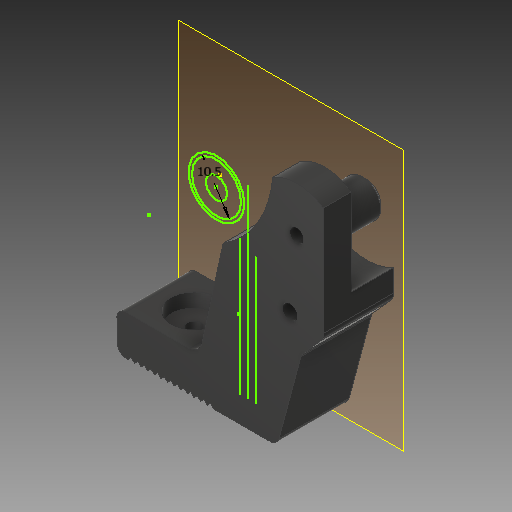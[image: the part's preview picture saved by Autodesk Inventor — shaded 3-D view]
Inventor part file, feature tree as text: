
AUTODESK INVENTOR PART (.ipt)
format: ipt  version: 2018 (Build 220112000, 112)  size: 333,824 bytes
history: native  units: in
note: dims shown in document units (in); Inventor stores cm internally (conversion verified against a paired STEP export)
features: extrude x10, sketch x10, fillet x2, reference x2, plane x1, chamfer x1, projected_geometry x1, other x1
ambient origin geometry x8: Origin, YZ Plane, XZ Plane, XY Plane, X Axis, Y Axis, Z Axis, Center Point
bodies: Solid1 (feature_tree)
feature tree (28):
  plane  "Work Plane1"
  extrude  "Extrusion1"  Depth=0.0787in
  sketch  "Sketch2"  dims[d2=0.0787in d4=0.126in]
  extrude  "Extrusion2"  Depth=0.126in
  chamfer  "Chamfer1"  Distance=0.0394in
  extrude  "Extrusion3"  Depth=0.0394in
  fillet  "Fillet1"  Radius=0.0394in
  extrude  "Extrusion4"  Depth=0.0394in
  extrude  "Extrusion5"  Depth=0.0394in
  extrude  "Extrusion6"  Depth=0.0394in
  extrude  "Extrusion7"  Depth=0.3937in TaperAngle=0.0deg
  sketch  "Sketch9"  dims[d11=0.0394in]
  fillet  "Fillet2"  Radius=0.9449in
  extrude  "Extrusion8"  Depth=0.3937in
  sketch  "Sketch1"  dims[d0=90.0deg d1=0.0787in]
  sketch  "Sketch3"  dims[d5=0.0394in]
  reference  "Reference9"
  sketch  "Sketch4"  dims[d6=135.0deg]
  reference  "Reference10"
  sketch  "Sketch5"  dims[d7=0.0394in]
  sketch  "Sketch6"  dims[d8=0.0394in]
  sketch  "Sketch7"  dims[d9=0.0394in]
  sketch  "Sketch8"  dims[d10=0.0394in]
  projected_geometry  "Projected Loop1"
  sketch  "Sketch10"  dims[d12=0.0394in d13=0.0394in d14=0.0394in d15=0.0394in d16=0.0394in d17=0.0394in d18=0.0394in d19=0.5906in d20=0.0in d21=0.9449in d22=0.311in d23=0.3543in d24=0.0in d25=0.0394in d26=0.0787in d27=45.0deg d28=0.5118in d29=180.0deg d30=105.0deg d31=0.0787in d32=0.3543in d33=0.0in d34=0.0787in d35=0.185in d36=90.0deg d37=0.0591in d38=0.0591in d39=0.126in d40=0.0591in d41=0.126in d42=0.3543in d43=0.3543in d44=0.0in d45=0.3543in d46=0.2244in d47=0.0in d48=90.0deg d49=0.3937in d50=90.0deg d51=0.0in d52=0.126in d53=0.1181in d54=0.0in d55=0.1181in d56=0.0in d57=0.4134in d58=0.0394in d59=0.1181in d60=0.3937in d61=0.0in]
  other  "<userpath>\OneDrive\Inventor\Beast 3D Printer\Extruder Assembly.iam"
  extrude  "Extruder Assembly.iam"  Depth=0.3937in TaperAngle=0.0deg
  extrude  "ExtruderArmwTensioningholeandadjBearing_fixed:1"  Depth=0.0394in TaperAngle=45.0deg
